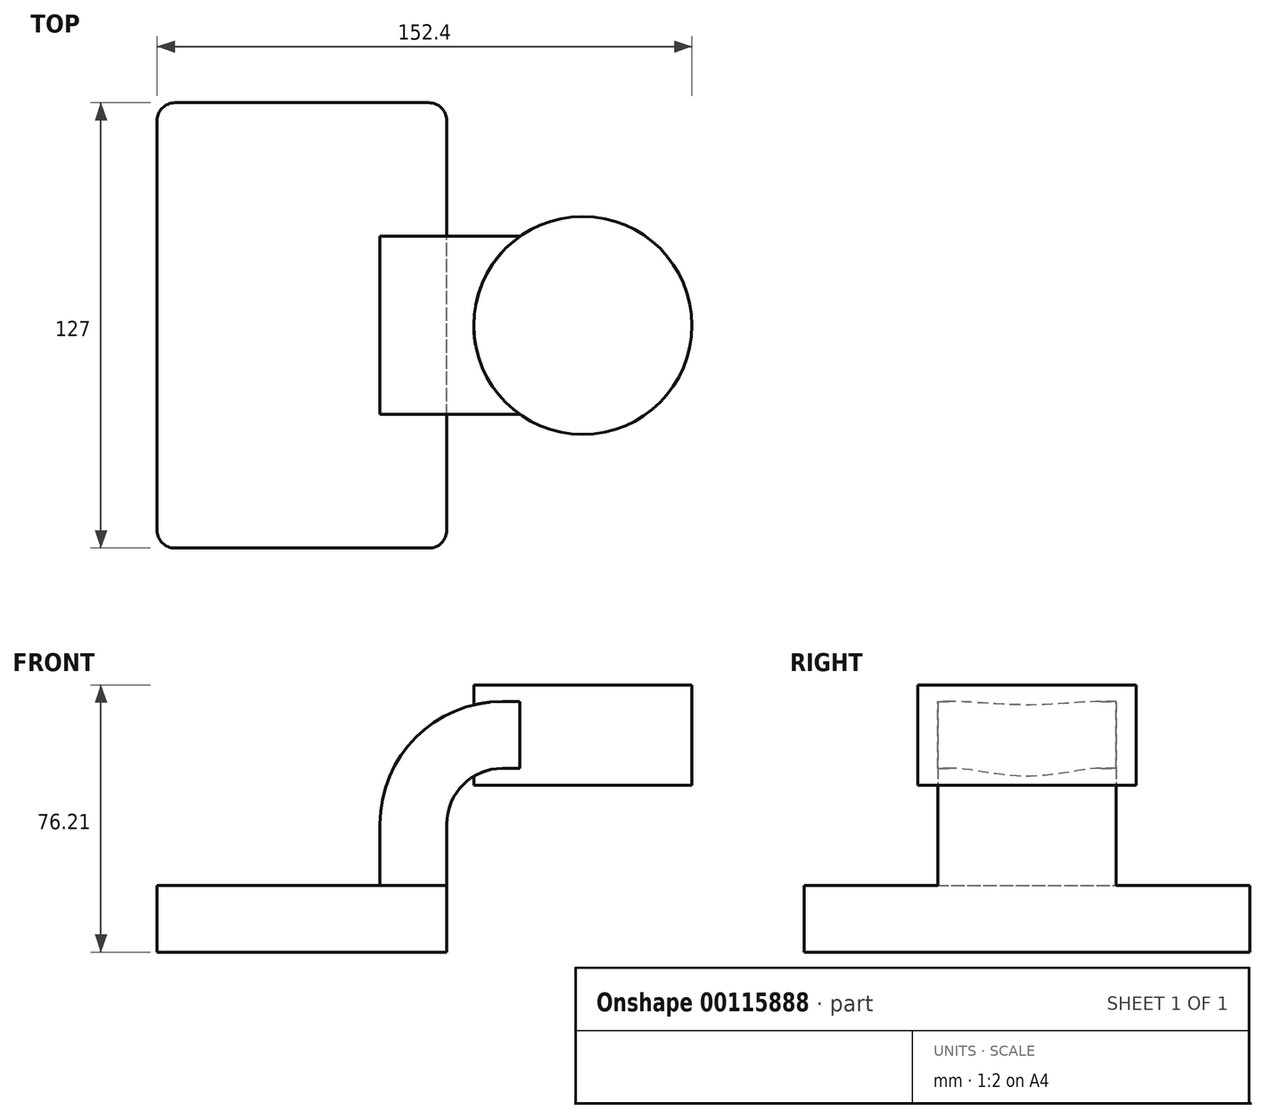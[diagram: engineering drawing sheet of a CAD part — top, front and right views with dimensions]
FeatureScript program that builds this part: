
annotation { "Feature Type Name" : "Feature", "Feature Type Description" : "" }
export const myFeature = defineFeature(function(context is Context, id is Id, definition is map)
    precondition{}
    {
        {
            var Q0;
            Q0=qCreatedBy(makeId("Front.planeOp"),FACE);
            var sketch = newSketch(context, id + "F0", { "sketchPlane" : qUnion([Q0])});
            skLineSegment(sketch, "E0.bottom", {"start": v(-41.28, 9.52) * mm, "end": v(41.27, 9.53) * mm});
            skLineSegment(sketch, "E0.top", {"start": v(-41.28, -9.53) * mm, "end": v(41.28, -9.53) * mm});
            skLineSegment(sketch, "E0.left", {"start": v(-41.28, 9.52) * mm, "end": v(-41.27, -9.53) * mm});
            skLineSegment(sketch, "E0.right", {"start": v(41.28, 9.53) * mm, "end": v(41.28, -9.52) * mm});
            skPoint(sketch, "E0.middle", {"position": v(0, 0) * mm});
            skLineSegment(sketch, "E1.bottom", {"start": v(60.33, 38.1) * mm, "end": v(111.12, 38.1) * mm});
            skLineSegment(sketch, "E1.top", {"start": v(60.32, 66.68) * mm, "end": v(111.12, 66.68) * mm});
            skLineSegment(sketch, "E1.left", {"start": v(60.33, 38.1) * mm, "end": v(60.32, 66.68) * mm});
            skLineSegment(sketch, "E1.right", {"start": v(111.12, 38.1) * mm, "end": v(111.12, 66.68) * mm});
            skPoint(sketch, "E1.middle", {"position": v(85.72, 52.39) * mm});
            skLineSegment(sketch, "E2", {"start": v(41.27, 9.53) * mm, "end": v(41.27, 27) * mm});
            skArc(sketch, "E3", {"start": v(41.27, 27) * mm, "mid": v(45.92, 38.23) * mm, "end": v(57.15, 42.88) * mm});
            skLineSegment(sketch, "E4", {"start": v(57.15, 42.88) * mm, "end": v(80.04, 42.88) * mm});
            skLineSegment(sketch, "E5.0", {"start": v(57.15, 61.93) * mm, "end": v(80.04, 61.93) * mm});
            skArc(sketch, "E5.1", {"start": v(22.23, 27) * mm, "mid": v(32.45, 51.7) * mm, "end": v(57.15, 61.93) * mm});
            skLineSegment(sketch, "E5.2", {"start": v(22.22, 9.53) * mm, "end": v(22.22, 27) * mm});
            skLineSegment(sketch, "E6", {"start": v(80.04, 66.68) * mm, "end": v(80.04, 38.1) * mm});
            skPoint(sketch, "E6.endSnap0", {"position": v(85.72, 38.1) * mm});
            skFitSpline(sketch, "E7", {"points": [v(-41.28, 9.53) * mm, v(57.15, 61.93) * mm], "startDerivative": vector(28.98, 112.87) * mm, "endDerivative": vector(145.7, -2.06) * mm});
            skSolve(sketch);
        }
        {
            var Q0;
            Q0=makeQuery(id+"F0.imprint","IMPRINT",FACE,{"disambiguationData":[TD([[makeQuery(id+"F0.imprint","IMPRINT",EDGE,{"derivedFrom":sQuery(id+"F0.wireOp",EDGE,"E0.top")}),1.0]])]});
            extrude(context, id + "F1", {"entities" : qUnion([Q0]), "endBound" : BoundingType.SYMMETRIC, "depth" : 127 * mm});
        }
        {
            var Q0;
            {var subQ1=sQuery(id+"F0.wireOp",EDGE,"E2");Q0=makeQuery(id+"F0.imprint","IMPRINT",FACE,{"disambiguationData":[TD([[makeQuery(id+"F0.imprint","IMPRINT",EDGE,{"derivedFrom":subQ1}),1.0]])]});}
            var Q1;
            {var subQ0=sQuery(id+"F0.wireOp",EDGE,"E4");var subQ1=sQuery(id+"F0.wireOp",EDGE,"E1.left");var subQ2=makeQuery(id+"F0.imprint","INTERSECT",VERTEX,{"derivedFrom":[subQ1,subQ0]});Q1=makeQuery(id+"F0.imprint","IMPRINT",FACE,{"disambiguationData":[TD([[makeQuery(id+"F0.imprint","IMPRINT",EDGE,{"disambiguationData":[TD([[subQ2,-1.0]])],"derivedFrom":subQ1}),-1.0]])]});}
            extrude(context, id + "F2", {"entities" : qUnion([Q0, Q1]), "operationType" : NewBodyOperationType.ADD, "endBound" : BoundingType.SYMMETRIC, "depth" : 50.8 * mm});
        }
        {
            var Q0;
            Q0=makeQuery(id+"F0.imprint","IMPRINT",FACE,{"disambiguationData":[TD([[makeQuery(id+"F0.imprint","IMPRINT",EDGE,{"derivedFrom":sQuery(id+"F0.wireOp",EDGE,"E5.1")}),1.0]])]});
            extrude(context, id + "F3", {"entities" : qUnion([Q0]), "operationType" : NewBodyOperationType.ADD, "endBound" : BoundingType.SYMMETRIC, "depth" : 15.88 * mm});
        }
        {
            var Q0;
            {var subQ0=sQuery(id+"F0.wireOp",EDGE,"E1.right");Q0=makeQuery(id+"F0.imprint","IMPRINT",FACE,{"disambiguationData":[TD([[makeQuery(id+"F0.imprint","IMPRINT",EDGE,{"derivedFrom":subQ0}),1.0]])]});}
            var Q1;
            Q1=sQuery(id+"F0.wireOp",EDGE,"E6");
            revolve(context, id + "F4", {"operationType" : NewBodyOperationType.ADD, "entities" : qUnion([Q0]), "axis" : qUnion([Q1]), "revolveType" : RevolveType.FULL});
        }
        {
            var Q0;
            Q0=makeQuery(id+"F1.opExtrude","CAP_EDGE",EDGE,{"disambiguationData":[OSD([sQuery(id+"F0.wireOp",EDGE,"E0.right")])],"isStart":true});
            var Q1;
            Q1=makeQuery(id+"F1.opExtrude","CAP_EDGE",EDGE,{"disambiguationData":[OSD([sQuery(id+"F0.wireOp",EDGE,"E0.left")])],"isStart":true});
            var Q2;
            Q2=makeQuery(id+"F1.opExtrude","CAP_EDGE",EDGE,{"disambiguationData":[OSD([sQuery(id+"F0.wireOp",EDGE,"E0.left")])],"isStart":false});
            var Q3;
            Q3=makeQuery(id+"F1.opExtrude","CAP_EDGE",EDGE,{"disambiguationData":[OSD([sQuery(id+"F0.wireOp",EDGE,"E0.right")])],"isStart":false});
            fillet(context, id + "F5", {"entities" : qUnion([Q0, Q1, Q2, Q3]), "radius" : 5.08 * mm, "tangentPropagation" : true, "allowEdgeOverflow" : false});
        }
    });
